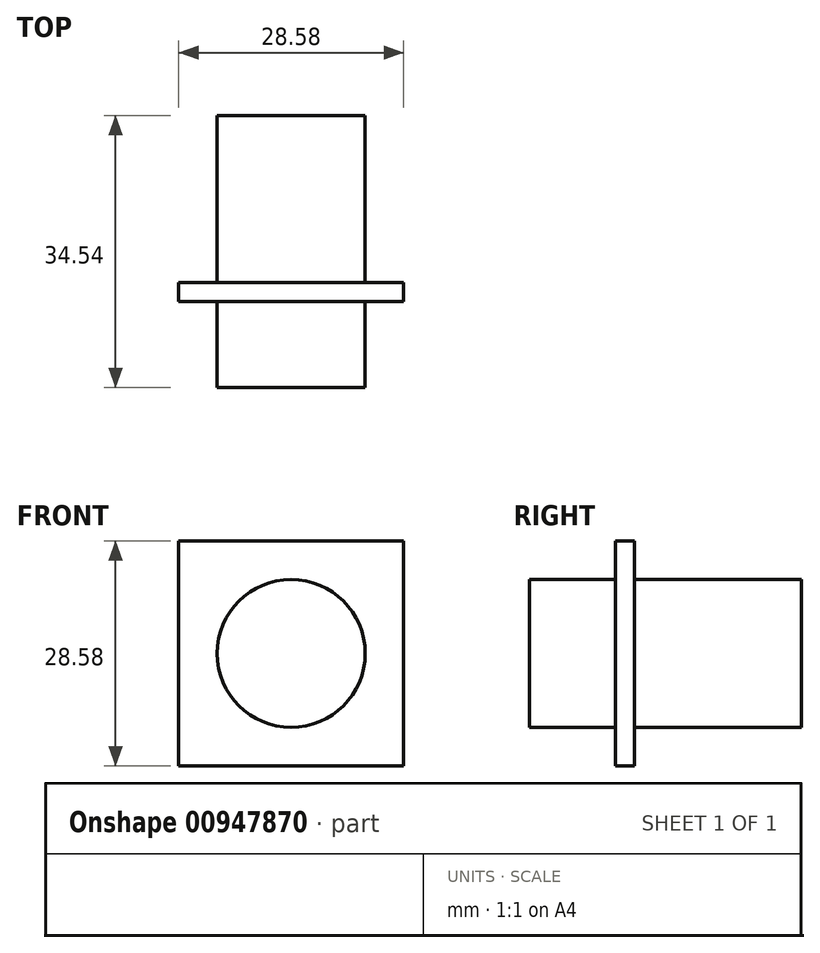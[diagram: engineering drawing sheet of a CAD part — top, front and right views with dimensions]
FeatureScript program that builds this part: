
annotation { "Feature Type Name" : "Feature", "Feature Type Description" : "" }
export const myFeature = defineFeature(function(context is Context, id is Id, definition is map)
    precondition{}
    {
        {
            var Q0;
            Q0=qCreatedBy(makeId("Front.planeOp"),FACE);
            var sketch = newSketch(context, id + "F0", { "sketchPlane" : qUnion([Q0])});
            skLineSegment(sketch, "E0.bottom", {"start": v(-14.29, 14.29) * mm, "end": v(14.29, 14.29) * mm});
            skLineSegment(sketch, "E0.top", {"start": v(-14.29, -14.29) * mm, "end": v(14.29, -14.29) * mm});
            skLineSegment(sketch, "E0.left", {"start": v(-14.29, 14.29) * mm, "end": v(-14.29, -14.29) * mm});
            skLineSegment(sketch, "E0.right", {"start": v(14.29, 14.29) * mm, "end": v(14.29, -14.29) * mm});
            skCircle(sketch, "E1", {"center": v(0, 0) * mm, "radius": 9.4 * mm});
            skSolve(sketch);
        }
        {
            var Q0;
            Q0=makeQuery(id+"F0.imprint","IMPRINT",FACE,{"disambiguationData":[TD([[makeQuery(id+"F0.imprint","IMPRINT",EDGE,{"derivedFrom":sQuery(id+"F0.wireOp",EDGE,"E0.bottom")}),-1.0]])]});
            extrude(context, id + "F1", {"entities" : qUnion([Q0]), "depth" : 2.4 * mm, "offsetDistance" : 25.4 * mm});
        }
        {
            var Q0;
            Q0=makeQuery(id+"F0.imprint","IMPRINT",FACE,{"disambiguationData":[TD([[makeQuery(id+"F0.imprint","IMPRINT",EDGE,{"derivedFrom":sQuery(id+"F0.wireOp",EDGE,"E1")}),1.0]])]});
            extrude(context, id + "F2", {"entities" : qUnion([Q0]), "operationType" : NewBodyOperationType.ADD, "depth" : 13.3 * mm, "offsetDistance" : 25.4 * mm, "hasSecondDirection" : true, "secondDirectionOppositeDirection" : true, "secondDirectionDepth" : 21.23 * mm});
        }
    });
